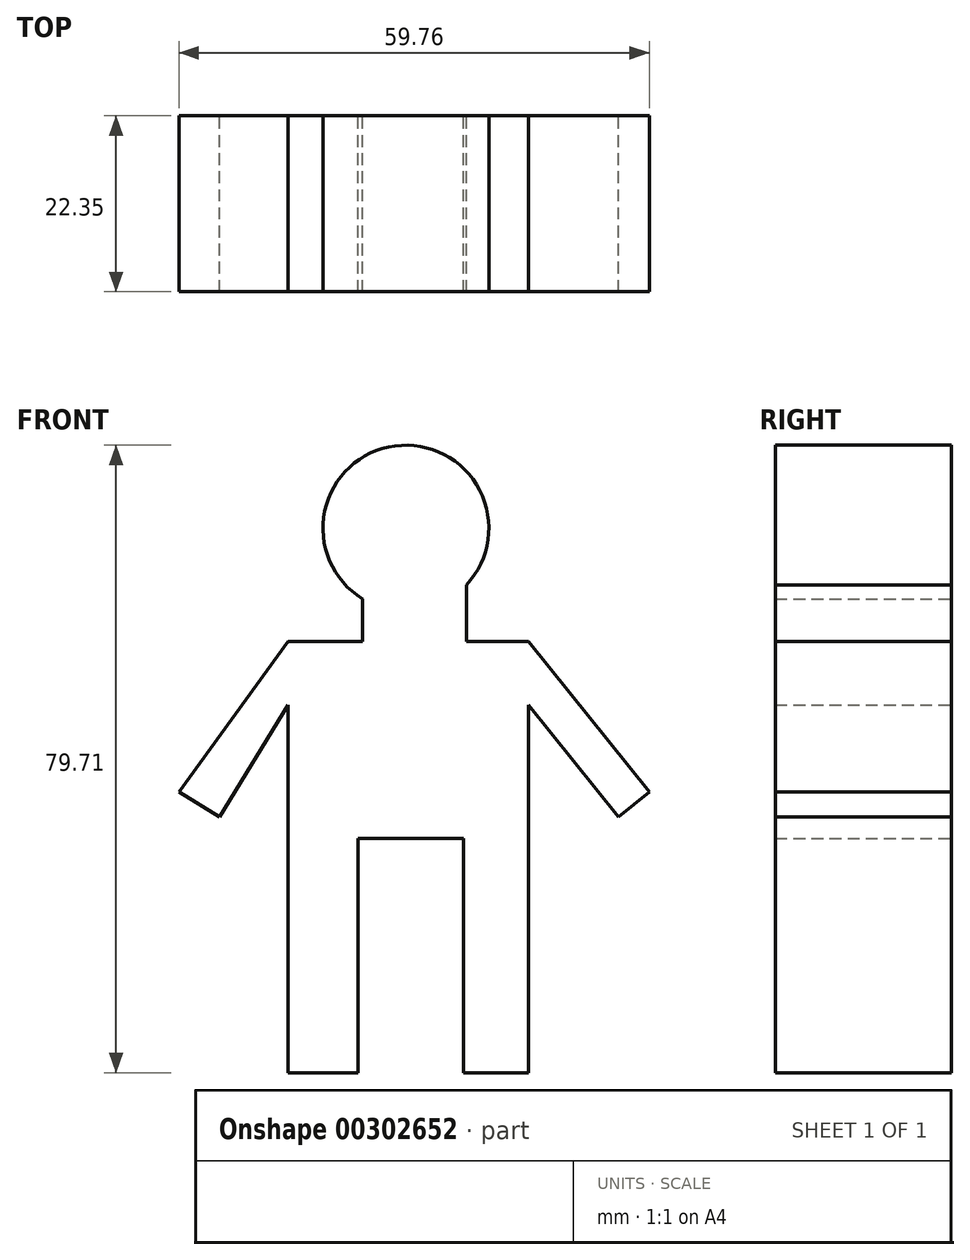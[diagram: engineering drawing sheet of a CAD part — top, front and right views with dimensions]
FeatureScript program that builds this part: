
annotation { "Feature Type Name" : "Feature", "Feature Type Description" : "" }
export const myFeature = defineFeature(function(context is Context, id is Id, definition is map)
    precondition{}
    {
        {
            var Q0;
            Q0=qCreatedBy(makeId("Front.planeOp"),FACE);
            var sketch = newSketch(context, id + "F0", { "sketchPlane" : qUnion([Q0])});
            skPoint(sketch, "E0.end.orphan", {"position": v(7.3, 29.76) * mm});
            skPoint(sketch, "E1.end.orphan", {"position": v(7.3, 0) * mm});
            skPoint(sketch, "E1.start.orphan", {"position": v(15.57, 0) * mm});
            skPoint(sketch, "E2.end.orphan", {"position": v(-6.1, 20.1) * mm});
            skPoint(sketch, "E3.end.orphan", {"position": v(-6.1, 29.76) * mm});
            skPoint(sketch, "E4.end.orphan", {"position": v(-14.98, 0) * mm});
            skPoint(sketch, "E4.start.orphan", {"position": v(-6.1, 0) * mm});
            skLineSegment(sketch, "E5", {"start": v(-14.98, 0) * mm, "end": v(-14.98, 29.95) * mm});
            skLineSegment(sketch, "E6", {"start": v(-14.98, 29.95) * mm, "end": v(-6.1, 29.76) * mm});
            skLineSegment(sketch, "E7", {"start": v(-6.1, 0) * mm, "end": v(-6.1, 29.76) * mm});
            skLineSegment(sketch, "E8", {"start": v(-6.1, 29.76) * mm, "end": v(7.3, 29.76) * mm});
            skLineSegment(sketch, "E9", {"start": v(7.3, 0) * mm, "end": v(7.3, 29.76) * mm});
            skLineSegment(sketch, "E10", {"start": v(7.3, 29.76) * mm, "end": v(15.57, 29.76) * mm});
            skLineSegment(sketch, "E11", {"start": v(15.57, 29.76) * mm, "end": v(15.57, 0) * mm});
            skLineSegment(sketch, "E12", {"start": v(15.57, 29.76) * mm, "end": v(15.57, 46.7) * mm});
            skLineSegment(sketch, "E13", {"start": v(15.57, 46.7) * mm, "end": v(27, 32.52) * mm});
            skLineSegment(sketch, "E14", {"start": v(27, 32.52) * mm, "end": v(30.93, 35.68) * mm});
            skLineSegment(sketch, "E15", {"start": v(30.93, 35.68) * mm, "end": v(15.57, 54.75) * mm});
            skLineSegment(sketch, "E16", {"start": v(15.57, 54.75) * mm, "end": v(7.69, 54.75) * mm});
            skLineSegment(sketch, "E17", {"start": v(7.69, 54.75) * mm, "end": v(7.69, 60.3) * mm});
            skLineSegment(sketch, "E18", {"start": v(-5.52, 60.3) * mm, "end": v(-5.52, 54.75) * mm});
            skLineSegment(sketch, "E19", {"start": v(-5.52, 54.75) * mm, "end": v(-14.98, 54.75) * mm});
            skLineSegment(sketch, "E20", {"start": v(-14.98, 54.75) * mm, "end": v(-14.98, 29.95) * mm});
            skLineSegment(sketch, "E21", {"start": v(-14.98, 46.7) * mm, "end": v(-23.65, 32.52) * mm});
            skLineSegment(sketch, "E22", {"start": v(-23.65, 32.52) * mm, "end": v(-28.83, 35.68) * mm});
            skLineSegment(sketch, "E23", {"start": v(-28.83, 35.68) * mm, "end": v(-14.98, 54.75) * mm});
            skLineSegment(sketch, "E24", {"start": v(-14.98, 0) * mm, "end": v(-6.1, 0) * mm});
            skLineSegment(sketch, "E25", {"start": v(7.3, 0) * mm, "end": v(15.57, 0) * mm});
            skPoint(sketch, "E26.0.midPoint", {"position": v(-7.49, 64.64) * mm});
            skPoint(sketch, "E26.cCircle.center.orphan", {"position": v(0, 69.17) * mm});
            skPoint(sketch, "E26.1.start.orphan", {"position": v(-7.77, 65.1) * mm});
            skPoint(sketch, "E26.49.end.orphan", {"position": v(-7.2, 64.17) * mm});
            skCircle(sketch, "E27", {"center": v(0, 69.17) * mm, "radius": 10.54 * mm});
            skLineSegment(sketch, "E28", {"start": v(7.69, 60.3) * mm, "end": v(7.69, 61.97) * mm});
            skSolve(sketch);
        }
        {
            var Q0;
            {var subQ4=sQuery(id+"F0.wireOp",EDGE,"E6");Q0=makeQuery(id+"F0.imprint","IMPRINT",FACE,{"disambiguationData":[TD([[makeQuery(id+"F0.imprint","IMPRINT",EDGE,{"derivedFrom":subQ4}),1.0]])]});}
            var Q1;
            {var subQ0=sQuery(id+"F0.wireOp",EDGE,"E27");var subQ1=makeQuery(id+"F0.imprint","INTERSECT",VERTEX,{"derivedFrom":[subQ0,sQuery(id+"F0.wireOp",EDGE,"E28")]});Q1=makeQuery(id+"F0.imprint","IMPRINT",FACE,{"disambiguationData":[TD([[makeQuery(id+"F0.imprint","IMPRINT",EDGE,{"disambiguationData":[TD([[subQ1,1.0]])],"derivedFrom":subQ0}),1.0]])]});}
            var Q2;
            {var subQ2=sQuery(id+"F0.wireOp",EDGE,"E21");Q2=makeQuery(id+"F0.imprint","IMPRINT",FACE,{"disambiguationData":[TD([[makeQuery(id+"F0.imprint","IMPRINT",EDGE,{"derivedFrom":subQ2}),-1.0]])]});}
            var Q3;
            Q3=makeQuery(id+"F0.imprint","IMPRINT",FACE,{"disambiguationData":[TD([[makeQuery(id+"F0.imprint","IMPRINT",EDGE,{"derivedFrom":sQuery(id+"F0.wireOp",EDGE,"E5")}),-1.0]])]});
            var Q4;
            Q4=makeQuery(id+"F0.imprint","IMPRINT",FACE,{"disambiguationData":[TD([[makeQuery(id+"F0.imprint","IMPRINT",EDGE,{"derivedFrom":sQuery(id+"F0.wireOp",EDGE,"E9")}),-1.0]])]});
            extrude(context, id + "F1", {"entities" : qUnion([Q0, Q1, Q2, Q3, Q4]), "depth" : 22.35 * mm});
        }
    });
